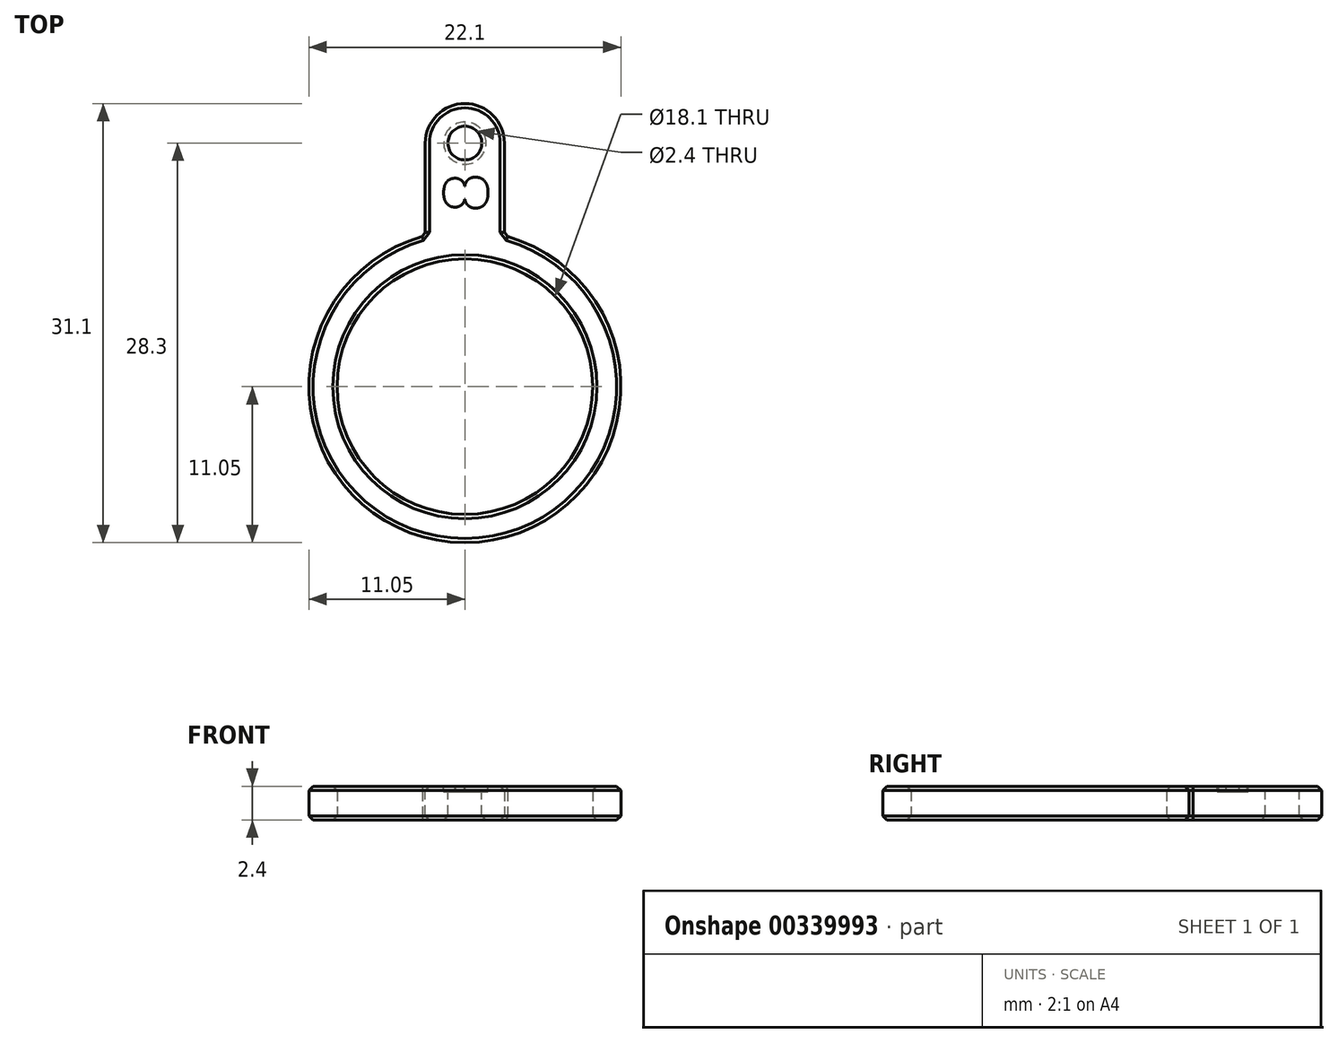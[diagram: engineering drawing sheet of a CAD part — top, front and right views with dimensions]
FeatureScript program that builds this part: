
annotation { "Feature Type Name" : "Feature", "Feature Type Description" : "" }
export const myFeature = defineFeature(function(context is Context, id is Id, definition is map)
    precondition{}
    {
        {
            var Q0;
            Q0=qCreatedBy(makeId("Top.planeOp"),FACE);
            var sketch = newSketch(context, id + "F0", { "sketchPlane" : qUnion([Q0])});
            skCircle(sketch, "E0", {"center": v(0, 0) * mm, "radius": 9.05 * mm});
            skCircle(sketch, "E1", {"center": v(0, 0) * mm, "radius": 11.05 * mm});
            skLineSegment(sketch, "E2.bottom", {"start": v(2.8, 2.05) * mm, "end": v(-2.8, 2.05) * mm});
            skLineSegment(sketch, "E2.top", {"start": v(2.8, 20.05) * mm, "end": v(-2.8, 20.05) * mm});
            skLineSegment(sketch, "E2.left", {"start": v(2.8, 2.05) * mm, "end": v(2.8, 20.05) * mm});
            skLineSegment(sketch, "E2.right", {"start": v(-2.8, 2.05) * mm, "end": v(-2.8, 20.05) * mm});
            skPoint(sketch, "E2.middle", {"position": v(0, 11.05) * mm});
            skSolve(sketch);
        }
        {
            var Q0;
            Q0=qSketchRegion(id+"F0",true);
            extrude(context, id + "F1", {"entities" : qUnion([Q0]), "depth" : 2.4 * mm});
        }
        {
            var Q0;
            Q0=makeQuery(id+"F1.opExtrude","SWEPT_EDGE",EDGE,{"disambiguationData":[OSD([sQuery(id+"F0.wireOp",EDGE,"E2.top"),sQuery(id+"F0.wireOp",EDGE,"E2.right")])]});
            var Q1;
            Q1=makeQuery(id+"F1.opExtrude","SWEPT_EDGE",EDGE,{"disambiguationData":[OSD([sQuery(id+"F0.wireOp",EDGE,"E2.top"),sQuery(id+"F0.wireOp",EDGE,"E2.left")])]});
            fillet(context, id + "F2", {"entities" : qUnion([Q0, Q1]), "radius" : 2.8 * mm, "tangentPropagation" : true, "allowEdgeOverflow" : false});
        }
        {
            var Q0;
            Q0=makeQuery(id+"F1.opExtrude","CAP_FACE",FACE,{"disambiguationData":[OSD([sQuery(id+"F0.wireOp",EDGE,"E0"),sQuery(id+"F0.wireOp",EDGE,"E1"),sQuery(id+"F0.wireOp",EDGE,"E2.top"),sQuery(id+"F0.wireOp",EDGE,"E2.left"),sQuery(id+"F0.wireOp",EDGE,"E2.right")])],"isStart":false});
            var sketch = newSketch(context, id + "F3", { "sketchPlane" : qUnion([Q0])});
            skCircle(sketch, "E3", {"center": v(0, 17.25) * mm, "radius": 1.2 * mm});
            skSolve(sketch);
        }
        {
            var Q0;
            Q0=qSketchRegion(id+"F3",true);
            extrude(context, id + "F4", {"entities" : qUnion([Q0]), "operationType" : NewBodyOperationType.REMOVE, "oppositeDirection" : true, "depth" : 25 * mm});
        }
        {
            var Q0;
            Q0=makeQuery(id+"F4.boolean.opBoolean","COPY",EDGE,{"derivedFrom":makeQuery(id+"F4.opExtrude","CAP_EDGE",EDGE,{"disambiguationData":[OSD([sQuery(id+"F3.wireOp",EDGE,"E3")])],"isStart":true})});
            var Q1;
            Q1=makeQuery(id+"F4.boolean.opBoolean","INTERSECT",EDGE,{"derivedFrom":[makeQuery(id+"F1.opExtrude","CAP_FACE",FACE,{"disambiguationData":[OSD([sQuery(id+"F0.wireOp",EDGE,"E0"),sQuery(id+"F0.wireOp",EDGE,"E1"),sQuery(id+"F0.wireOp",EDGE,"E2.top"),sQuery(id+"F0.wireOp",EDGE,"E2.left"),sQuery(id+"F0.wireOp",EDGE,"E2.right")])],"isStart":true}),makeQuery(id+"F4.opExtrude","SWEPT_FACE",FACE,{"disambiguationData":[OSD([sQuery(id+"F3.wireOp",EDGE,"E3")])]})]});
            var Q2;
            {var subQ0=sQuery(id+"F0.wireOp",EDGE,"E2.right");var subQ1=sQuery(id+"F0.wireOp",EDGE,"E2.top");Q2=makeQuery(id+"F2.opFillet","BLEND_EDGE",EDGE,{"blendedFrom":[makeQuery(id+"F1.opExtrude","SWEPT_EDGE",EDGE,{"disambiguationData":[OSD([subQ1,subQ0])]}),makeQuery(id+"F1.opExtrude","CAP_FACE",FACE,{"disambiguationData":[OSD([sQuery(id+"F0.wireOp",EDGE,"E0"),sQuery(id+"F0.wireOp",EDGE,"E1"),subQ1,sQuery(id+"F0.wireOp",EDGE,"E2.left"),subQ0])],"isStart":true})],"blendedInto":[makeQuery(id+"F1.opExtrude","CAP_FACE",FACE,{"disambiguationData":[OSD([sQuery(id+"F0.wireOp",EDGE,"E0"),sQuery(id+"F0.wireOp",EDGE,"E1"),subQ1,sQuery(id+"F0.wireOp",EDGE,"E2.left"),subQ0])],"isStart":true})]});}
            var Q3;
            {var subQ0=sQuery(id+"F0.wireOp",EDGE,"E2.right");var subQ1=sQuery(id+"F0.wireOp",EDGE,"E2.top");Q3=makeQuery(id+"F2.opFillet","BLEND_EDGE",EDGE,{"blendedFrom":[makeQuery(id+"F1.opExtrude","SWEPT_EDGE",EDGE,{"disambiguationData":[OSD([subQ1,subQ0])]}),makeQuery(id+"F1.opExtrude","CAP_FACE",FACE,{"disambiguationData":[OSD([sQuery(id+"F0.wireOp",EDGE,"E0"),sQuery(id+"F0.wireOp",EDGE,"E1"),subQ1,sQuery(id+"F0.wireOp",EDGE,"E2.left"),subQ0])],"isStart":false})],"blendedInto":[makeQuery(id+"F1.opExtrude","CAP_FACE",FACE,{"disambiguationData":[OSD([sQuery(id+"F0.wireOp",EDGE,"E0"),sQuery(id+"F0.wireOp",EDGE,"E1"),subQ1,sQuery(id+"F0.wireOp",EDGE,"E2.left"),subQ0])],"isStart":false})]});}
            var Q4;
            Q4=makeQuery(id+"F1.opExtrude","CAP_EDGE",EDGE,{"disambiguationData":[OSD([sQuery(id+"F0.wireOp",EDGE,"E1")])],"isStart":false});
            var Q5;
            Q5=makeQuery(id+"F1.opExtrude","CAP_EDGE",EDGE,{"disambiguationData":[OSD([sQuery(id+"F0.wireOp",EDGE,"E1")])],"isStart":true});
            var Q6;
            Q6=makeQuery(id+"F1.opExtrude","SWEPT_EDGE",EDGE,{"disambiguationData":[OSD([sQuery(id+"F0.wireOp",EDGE,"E1"),sQuery(id+"F0.wireOp",EDGE,"E2.left")])]});
            var Q7;
            Q7=makeQuery(id+"F1.opExtrude","SWEPT_EDGE",EDGE,{"disambiguationData":[OSD([sQuery(id+"F0.wireOp",EDGE,"E1"),sQuery(id+"F0.wireOp",EDGE,"E2.right")])]});
            var Q8;
            Q8=makeQuery(id+"F1.opExtrude","CAP_EDGE",EDGE,{"disambiguationData":[OSD([sQuery(id+"F0.wireOp",EDGE,"E0")])],"isStart":true});
            var Q9;
            Q9=makeQuery(id+"F1.opExtrude","CAP_EDGE",EDGE,{"disambiguationData":[OSD([sQuery(id+"F0.wireOp",EDGE,"E0")])],"isStart":false});
            chamfer(context, id + "F5", {"entities" : qUnion([Q0, Q1, Q2, Q3, Q4, Q5, Q6, Q7, Q8, Q9]), "width" : 0.3 * mm, "tangentPropagation" : true});
        }
        {
            var Q0;
            Q0=makeQuery(id+"F1.opExtrude","CAP_FACE",FACE,{"disambiguationData":[OSD([sQuery(id+"F0.wireOp",EDGE,"E0"),sQuery(id+"F0.wireOp",EDGE,"E1"),sQuery(id+"F0.wireOp",EDGE,"E2.top"),sQuery(id+"F0.wireOp",EDGE,"E2.left"),sQuery(id+"F0.wireOp",EDGE,"E2.right")])],"isStart":false});
            var sketch = newSketch(context, id + "F6", { "sketchPlane" : qUnion([Q0])});
            skText(sketch, "E4", { "text": "8", "fontName": "Arimo-Bold.ttf"});
            skLineSegment(sketch, "E5", {"start": v(0, 12.5) * mm, "end": v(0, 0) * mm});
            skPoint(sketch, "E5.endSnap0", {"position": v(0, 12.5) * mm});
            const initialGuessF6  = {"E4": [0.0016, 0.0125, 0, 1, 0.0032]};
            skSetInitialGuess(sketch, initialGuessF6);
            skSolve(sketch);
        }
        {
            var Q0;
            Q0=qSketchRegion(id+"F6",true);
            var Q1;
            Q1=makeQuery(id+"F6.imprint","IMPRINT",FACE,{"disambiguationData":[TD([[makeQuery(id+"F6.imprint","IMPRINT",EDGE,{"derivedFrom":sQuery(id+"F6.wireOp",EDGE,"E4.sketch_text.stroke-18")}),1.0]])]});
            var Q2;
            Q2=makeQuery(id+"F6.imprint","IMPRINT",FACE,{"disambiguationData":[TD([[makeQuery(id+"F6.imprint","IMPRINT",EDGE,{"derivedFrom":sQuery(id+"F6.wireOp",EDGE,"E4.sketch_text.stroke-24")}),1.0]])]});
            extrude(context, id + "F7", {"entities" : qUnion([Q0, Q1, Q2]), "operationType" : NewBodyOperationType.REMOVE, "oppositeDirection" : true, "depth" : 0.4 * mm});
        }
    });
